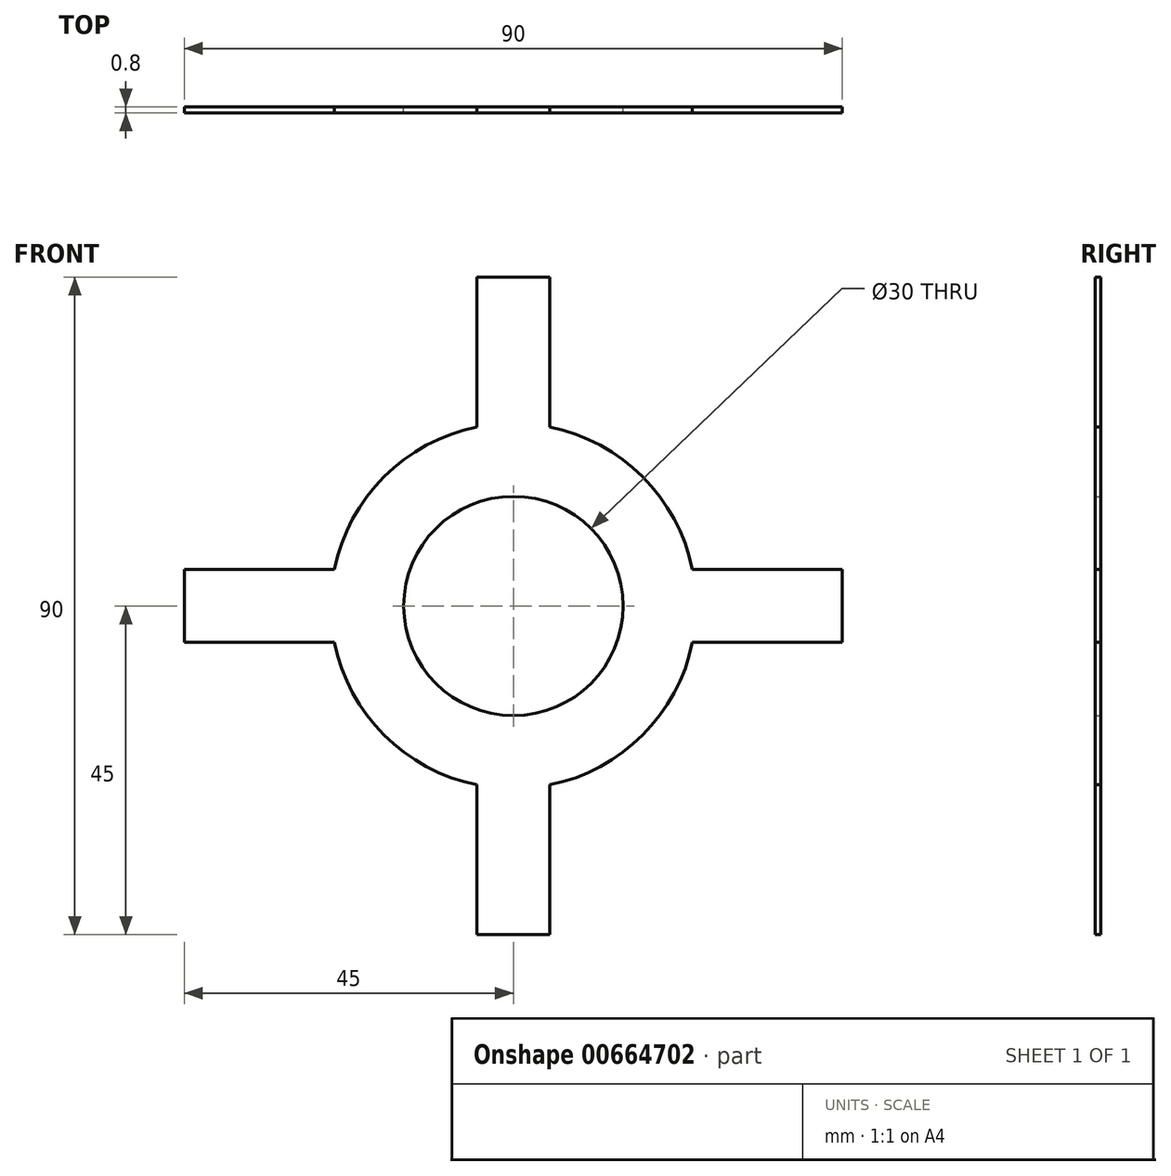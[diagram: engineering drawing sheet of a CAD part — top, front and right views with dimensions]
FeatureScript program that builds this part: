
annotation { "Feature Type Name" : "Feature", "Feature Type Description" : "" }
export const myFeature = defineFeature(function(context is Context, id is Id, definition is map)
    precondition{}
    {
        {
            var Q0;
            Q0=qCreatedBy(makeId("Front.planeOp"),FACE);
            var sketch = newSketch(context, id + "F0", { "sketchPlane" : qUnion([Q0])});
            skCircle(sketch, "E0", {"center": v(0, 0) * mm, "radius": 15 * mm});
            skArc(sketch, "E1", {"start": v(-24.5, -5) * mm, "mid": v(-17.68, -17.68) * mm, "end": v(-5, -24.5) * mm});
            skLineSegment(sketch, "E2.bottom", {"start": v(-5, 45) * mm, "end": v(5, 45) * mm});
            skLineSegment(sketch, "E2.top", {"start": v(-5, -45) * mm, "end": v(5, -45) * mm});
            skLineSegment(sketch, "E2.left", {"start": v(-5, 45) * mm, "end": v(-5, 24.5) * mm});
            skLineSegment(sketch, "E2.right", {"start": v(5, 45) * mm, "end": v(5, 24.5) * mm});
            skLineSegment(sketch, "E3.bottom", {"start": v(-45, 5) * mm, "end": v(-24.5, 5) * mm});
            skLineSegment(sketch, "E3.top", {"start": v(-45, -5) * mm, "end": v(-24.5, -5) * mm});
            skLineSegment(sketch, "E3.left", {"start": v(-45, 5) * mm, "end": v(-45, -5) * mm});
            skLineSegment(sketch, "E3.right", {"start": v(45, 5) * mm, "end": v(45, -5) * mm});
            skLineSegment(sketch, "E4.trimOffspring", {"start": v(24.5, 5) * mm, "end": v(45, 5) * mm});
            skLineSegment(sketch, "E5.trimOffspring", {"start": v(24.5, -5) * mm, "end": v(45, -5) * mm});
            skLineSegment(sketch, "E6.trimOffspring", {"start": v(-5, -24.5) * mm, "end": v(-5, -45) * mm});
            skArc(sketch, "E7.trimOffspring", {"start": v(-5, 24.5) * mm, "mid": v(-17.68, 17.68) * mm, "end": v(-24.5, 5) * mm});
            skLineSegment(sketch, "E8.trimOffspring", {"start": v(5, -24.5) * mm, "end": v(5, -45) * mm});
            skArc(sketch, "E9.trimOffspring", {"start": v(24.5, 5) * mm, "mid": v(17.68, 17.68) * mm, "end": v(5, 24.5) * mm});
            skArc(sketch, "E10.trimOffspring", {"start": v(5, -24.5) * mm, "mid": v(17.68, -17.68) * mm, "end": v(24.5, -5) * mm});
            skSolve(sketch);
        }
        {
            var Q0;
            Q0 = qSketchRegion(id + "F0", true);
            extrude(context, id + "F1", {"entities" : qUnion([Q0]), "depth" : 0.8 * mm, "offsetDistance" : 25 * mm});
        }
    });
